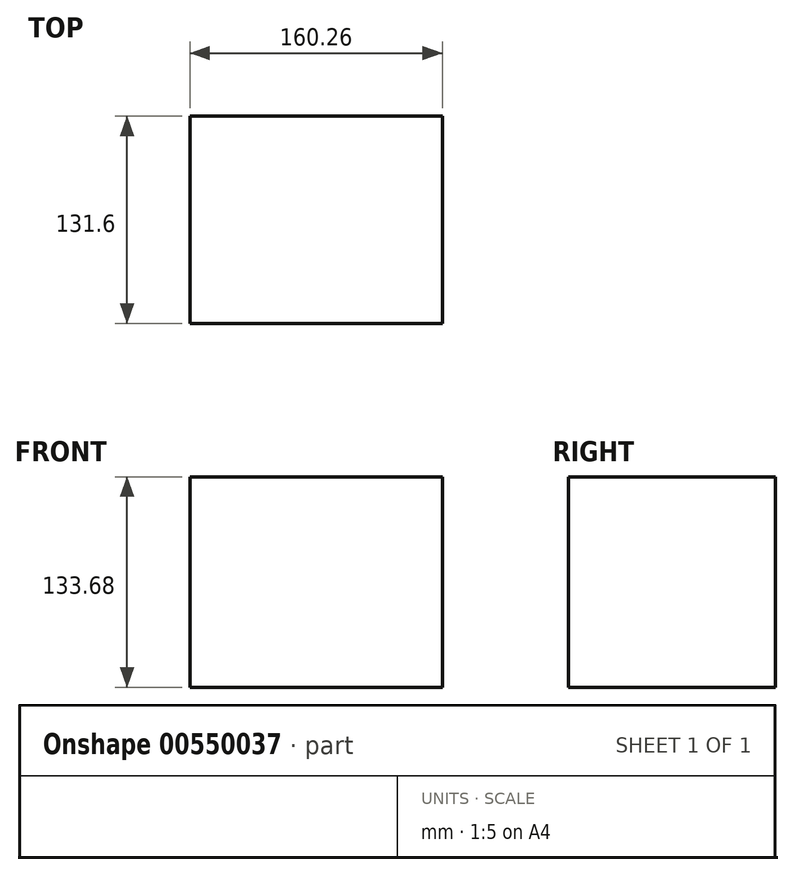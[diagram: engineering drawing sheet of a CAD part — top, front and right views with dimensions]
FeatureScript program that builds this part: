
annotation { "Feature Type Name" : "Feature", "Feature Type Description" : "" }
export const myFeature = defineFeature(function(context is Context, id is Id, definition is map)
    precondition{}
    {
        {
            var Q0;
            Q0=qCreatedBy(makeId("Front.planeOp"),FACE);
            var sketch = newSketch(context, id + "F0", { "sketchPlane" : qUnion([Q0])});
            skLineSegment(sketch, "E0.bottom", {"start": v(-80.97, -59.08) * mm, "end": v(79.29, -59.08) * mm});
            skLineSegment(sketch, "E0.top", {"start": v(-80.97, 49.6) * mm, "end": v(79.29, 49.6) * mm});
            skLineSegment(sketch, "E0.left", {"start": v(-80.97, -59.08) * mm, "end": v(-80.97, 49.6) * mm});
            skLineSegment(sketch, "E0.right", {"start": v(79.29, -59.08) * mm, "end": v(79.29, 49.6) * mm});
            skSolve(sketch);
        }
        {
            var Q0;
            Q0 = qSketchRegion(id + "F0", true);
            extrude(context, id + "F1", {"entities" : qUnion([Q0]), "depth" : 131.6 * mm, "offsetDistance" : 25 * mm});
        }
        {
            var Q0;
            Q0=makeQuery(id+"F1.opExtrude","SWEPT_FACE",FACE,{"disambiguationData":[OSD([sQuery(id+"F0.wireOp",EDGE,"E0.top")])]});
            extrude(context, id + "F2", {"entities" : qUnion([Q0]), "operationType" : NewBodyOperationType.ADD, "depth" : 25 * mm, "offsetDistance" : 25 * mm});
        }
    });
